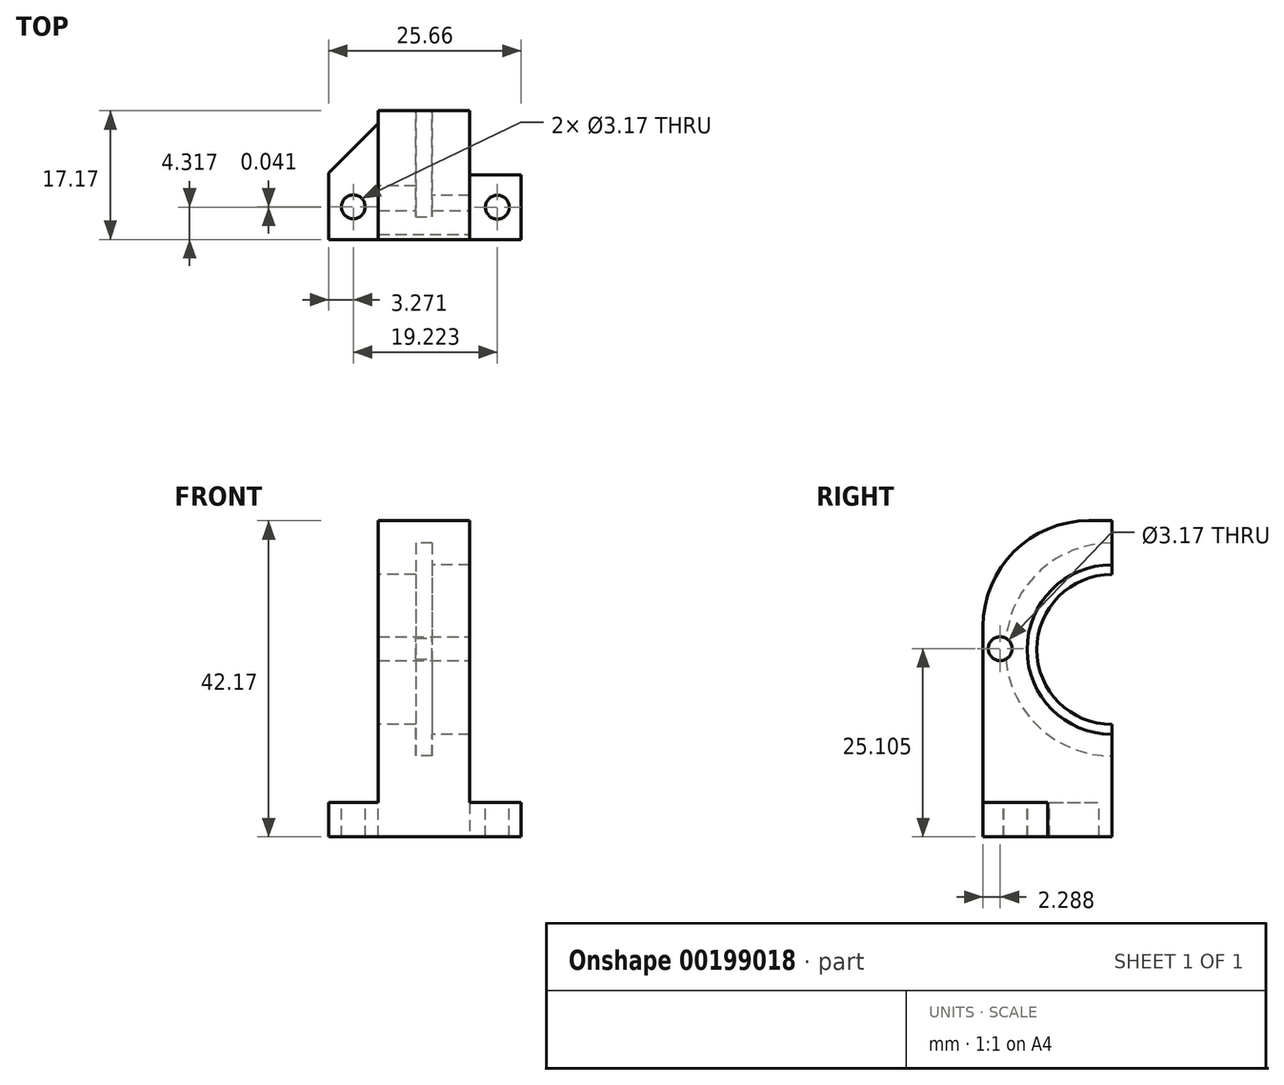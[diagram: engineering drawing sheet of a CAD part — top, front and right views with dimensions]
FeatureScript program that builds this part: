
annotation { "Feature Type Name" : "Feature", "Feature Type Description" : "" }
export const myFeature = defineFeature(function(context is Context, id is Id, definition is map)
    precondition{}
    {
        {
            var Q0;
            Q0=qCreatedBy(makeId("Right.planeOp"),FACE);
            var sketch = newSketch(context, id + "F0", { "sketchPlane" : qUnion([Q0])});
            skLineSegment(sketch, "E0", {"start": v(0, 0) * mm, "end": v(0, 15) * mm});
            skLineSegment(sketch, "E1", {"start": v(0, 0) * mm, "end": v(-17.17, 0) * mm});
            skLineSegment(sketch, "E2", {"start": v(-17.17, 0) * mm, "end": v(-17.17, 42.17) * mm});
            skArc(sketch, "E3", {"start": v(0, 35) * mm, "mid": v(-10, 25) * mm, "end": v(0, 15) * mm});
            skLineSegment(sketch, "E4", {"start": v(-17.17, 42.17) * mm, "end": v(0, 42.17) * mm});
            skLineSegment(sketch, "E5", {"start": v(0, 42.17) * mm, "end": v(0, 35) * mm});
            skSolve(sketch);
        }
        {
            var Q0;
            Q0=makeQuery(id+"F0.imprint","IMPRINT",FACE,{"disambiguationData":[TD([[makeQuery(id+"F0.imprint","IMPRINT",EDGE,{"derivedFrom":sQuery(id+"F0.wireOp",EDGE,"E0")}),1.0]])]});
            extrude(context, id + "F1", {"entities" : qUnion([Q0]), "depth" : 5 * mm});
        }
        {
            var Q0;
            Q0=makeQuery(id+"F1.opExtrude","CAP_FACE",FACE,{"disambiguationData":[OSD([sQuery(id+"F0.wireOp",EDGE,"E0"),sQuery(id+"F0.wireOp",EDGE,"E1"),sQuery(id+"F0.wireOp",EDGE,"E2"),sQuery(id+"F0.wireOp",EDGE,"E3"),sQuery(id+"F0.wireOp",EDGE,"E4"),sQuery(id+"F0.wireOp",EDGE,"E5")])],"isStart":false});
            var sketch = newSketch(context, id + "F2", { "sketchPlane" : qUnion([Q0])});
            skArc(sketch, "E6", {"start": v(0, 39.2) * mm, "mid": v(-14.2, 25) * mm, "end": v(0, 10.8) * mm});
            skSolve(sketch);
        }
        {
            var Q0;
            {var subQ2=sQuery(id+"F2.wireOp",EDGE,"E6");Q0=makeQuery(id+"F2.imprint","IMPRINT",FACE,{"disambiguationData":[TD([[makeQuery(id+"F2.imprint","IMPRINT",EDGE,{"derivedFrom":subQ2}),-1.0]])]});}
            extrude(context, id + "F3", {"entities" : qUnion([Q0]), "operationType" : NewBodyOperationType.ADD, "depth" : 2.2 * mm});
        }
        {
            var Q0;
            Q0=makeQuery(id+"F3.opExtrude","CAP_FACE",FACE,{"disambiguationData":[OSD([sQuery(id+"F0.wireOp",EDGE,"E0"),sQuery(id+"F0.wireOp",EDGE,"E1"),sQuery(id+"F0.wireOp",EDGE,"E2"),sQuery(id+"F0.wireOp",EDGE,"E4"),sQuery(id+"F0.wireOp",EDGE,"E5"),sQuery(id+"F2.wireOp",EDGE,"E6")])],"isStart":false});
            var sketch = newSketch(context, id + "F4", { "sketchPlane" : qUnion([Q0])});
            skArc(sketch, "E7", {"start": v(0, 36.3) * mm, "mid": v(-11.3, 25) * mm, "end": v(0, 13.7) * mm});
            skPoint(sketch, "E7.endSnap0", {"position": v(0, 40.68) * mm});
            skLineSegment(sketch, "E8", {"start": v(0, 36.3) * mm, "end": v(0, 39.2) * mm});
            skLineSegment(sketch, "E9", {"start": v(0, 13.7) * mm, "end": v(0, 10.8) * mm});
            skSolve(sketch);
        }
        {
            var Q0;
            Q0=makeQuery(id+"F4.imprint","IMPRINT",FACE,{"disambiguationData":[TD([[makeQuery(id+"F4.imprint","IMPRINT",EDGE,{"derivedFrom":makeQuery(id+"F3.opExtrude","CAP_EDGE",EDGE,{"disambiguationData":[OSD([sQuery(id+"F2.wireOp",EDGE,"E6")])],"isStart":false})}),-1.0]])]});
            var Q1;
            Q1=makeQuery(id+"F4.imprint","IMPRINT",FACE,{"disambiguationData":[TD([[makeQuery(id+"F4.imprint","IMPRINT",EDGE,{"derivedFrom":sQuery(id+"F4.wireOp",EDGE,"E7")}),-1.0]])]});
            extrude(context, id + "F5", {"entities" : qUnion([Q0, Q1]), "operationType" : NewBodyOperationType.ADD, "depth" : 5 * mm});
        }
        {
            var Q0;
            {var subQ0=sQuery(id+"F0.wireOp",EDGE,"E4");var subQ1=sQuery(id+"F0.wireOp",EDGE,"E2");Q0=makeQuery(id+"F5.boolean.opBoolean","MERGE",EDGE,{"derivedFrom":[makeQuery(id+"F3.boolean.opBoolean","MERGE",EDGE,{"derivedFrom":[makeQuery(id+"F1.opExtrude","SWEPT_EDGE",EDGE,{"disambiguationData":[OSD([subQ1,subQ0])]}),makeQuery(id+"F3.opExtrude","SWEPT_EDGE",EDGE,{"disambiguationData":[OSD([subQ1,subQ0])]})]}),makeQuery(id+"F5.opExtrude","SWEPT_EDGE",EDGE,{"disambiguationData":[OSD([subQ1,subQ0])]})]});}
            fillet(context, id + "F6", {"entities" : qUnion([Q0]), "radius" : 14.1 * mm, "tangentPropagation" : true, "allowEdgeOverflow" : false});
        }
        {
            var Q0;
            Q0=makeQuery(id+"F5.opExtrude","CAP_FACE",FACE,{"disambiguationData":[OSD([sQuery(id+"F0.wireOp",EDGE,"E0"),sQuery(id+"F0.wireOp",EDGE,"E1"),sQuery(id+"F0.wireOp",EDGE,"E2"),sQuery(id+"F0.wireOp",EDGE,"E4"),sQuery(id+"F0.wireOp",EDGE,"E5"),sQuery(id+"F4.wireOp",EDGE,"E7"),sQuery(id+"F4.wireOp",EDGE,"E8"),sQuery(id+"F4.wireOp",EDGE,"E9")])],"isStart":false});
            var sketch = newSketch(context, id + "F7", { "sketchPlane" : qUnion([Q0])});
            skLineSegment(sketch, "E10", {"start": v(-17.17, 4.57) * mm, "end": v(-8.53, 4.57) * mm});
            skLineSegment(sketch, "E11", {"start": v(-8.53, 4.57) * mm, "end": v(-8.53, 0) * mm});
            skSolve(sketch);
        }
        {
            var Q0;
            {var subQ0=sQuery(id+"F7.wireOp",EDGE,"E10");Q0=makeQuery(id+"F7.imprint","IMPRINT",FACE,{"disambiguationData":[TD([[makeQuery(id+"F7.imprint","IMPRINT",EDGE,{"derivedFrom":subQ0}),-1.0]])]});}
            extrude(context, id + "F8", {"entities" : qUnion([Q0]), "operationType" : NewBodyOperationType.ADD, "depth" : 6.86 * mm});
        }
        {
            var Q0;
            Q0=makeQuery(id+"F8.opExtrude","SWEPT_FACE",FACE,{"disambiguationData":[OSD([sQuery(id+"F7.wireOp",EDGE,"E10")])]});
            var sketch = newSketch(context, id + "F9", { "sketchPlane" : qUnion([Q0])});
            skCircle(sketch, "E12", {"center": v(15.9, -12.85) * mm, "radius": 1.59 * mm});
            skPoint(sketch, "E12.centerSnap0", {"position": v(19.06, -12.85) * mm});
            skSolve(sketch);
        }
        {
            var Q0;
            Q0=makeQuery(id+"F8.opExtrude","CAP_FACE",FACE,{"disambiguationData":[OSD([sQuery(id+"F0.wireOp",EDGE,"E1"),sQuery(id+"F0.wireOp",EDGE,"E2"),sQuery(id+"F7.wireOp",EDGE,"E10"),sQuery(id+"F7.wireOp",EDGE,"E11")])],"isStart":false});
            extrude(context, id + "F10", {"entities" : qUnion([Q0]), "operationType" : NewBodyOperationType.ADD, "oppositeDirection" : true, "depth" : 25.65 * mm});
        }
        {
            var Q0;
            Q0=makeQuery(id+"F9.imprint","IMPRINT",FACE,{"disambiguationData":[TD([[makeQuery(id+"F9.imprint","IMPRINT",EDGE,{"derivedFrom":sQuery(id+"F9.wireOp",EDGE,"E12")}),1.0]])]});
            extrude(context, id + "F11", {"entities" : qUnion([Q0]), "operationType" : NewBodyOperationType.REMOVE, "oppositeDirection" : true, "depth" : 26.92 * mm});
        }
        {
            var Q0;
            Q0=makeQuery(id+"F10.opExtrude","SWEPT_FACE",FACE,{"disambiguationData":[OSD([sQuery(id+"F7.wireOp",EDGE,"E10")])]});
            var sketch = newSketch(context, id + "F12", { "sketchPlane" : qUnion([Q0])});
            skCircle(sketch, "E13", {"center": v(-3.33, -12.81) * mm, "radius": 1.59 * mm});
            skSolve(sketch);
        }
        {
            var Q0;
            Q0=makeQuery(id+"F12.imprint","IMPRINT",FACE,{"disambiguationData":[TD([[makeQuery(id+"F12.imprint","IMPRINT",EDGE,{"derivedFrom":sQuery(id+"F12.wireOp",EDGE,"E13")}),1.0]])]});
            extrude(context, id + "F13", {"entities" : qUnion([Q0]), "operationType" : NewBodyOperationType.REMOVE, "oppositeDirection" : true, "depth" : 9.58 * mm});
        }
        {
            var Q0;
            Q0=makeQuery(id+"F8.opExtrude","CAP_EDGE",EDGE,{"disambiguationData":[OSD([sQuery(id+"F7.wireOp",EDGE,"E11")])],"isStart":true});
            var Q1;
            Q1=makeQuery(id+"F10.boolean.opBoolean","INTERSECT",EDGE,{"derivedFrom":[makeQuery(id+"F1.opExtrude","CAP_FACE",FACE,{"disambiguationData":[OSD([sQuery(id+"F0.wireOp",EDGE,"E0"),sQuery(id+"F0.wireOp",EDGE,"E1"),sQuery(id+"F0.wireOp",EDGE,"E2"),sQuery(id+"F0.wireOp",EDGE,"E3"),sQuery(id+"F0.wireOp",EDGE,"E4"),sQuery(id+"F0.wireOp",EDGE,"E5")])],"isStart":true}),makeQuery(id+"F10.opExtrude","SWEPT_FACE",FACE,{"disambiguationData":[OSD([sQuery(id+"F7.wireOp",EDGE,"E11")])]})]});
            chamfer(context, id + "F14", {"entities" : qUnion([Q0, Q1]), "width" : 6.86 * mm, "tangentPropagation" : true});
        }
        {
            var Q0;
            {var subQ11=sQuery(id+"F7.wireOp",EDGE,"E10");Q0=makeQuery(id+"F7.imprint","IMPRINT",FACE,{"disambiguationData":[TD([[makeQuery(id+"F7.imprint","IMPRINT",EDGE,{"derivedFrom":subQ11}),1.0]])]});}
            var sketch = newSketch(context, id + "F15", { "sketchPlane" : qUnion([Q0])});
            skCircle(sketch, "E14", {"center": v(-14.88, 25.1) * mm, "radius": 1.59 * mm});
            skSolve(sketch);
        }
        {
            var Q0;
            Q0=makeQuery(id+"F15.imprint","IMPRINT",FACE,{"disambiguationData":[TD([[makeQuery(id+"F15.imprint","IMPRINT",EDGE,{"derivedFrom":sQuery(id+"F15.wireOp",EDGE,"E14")}),1.0]])]});
            extrude(context, id + "F16", {"entities" : qUnion([Q0]), "operationType" : NewBodyOperationType.REMOVE, "oppositeDirection" : true, "depth" : 18.03 * mm});
        }
    });
